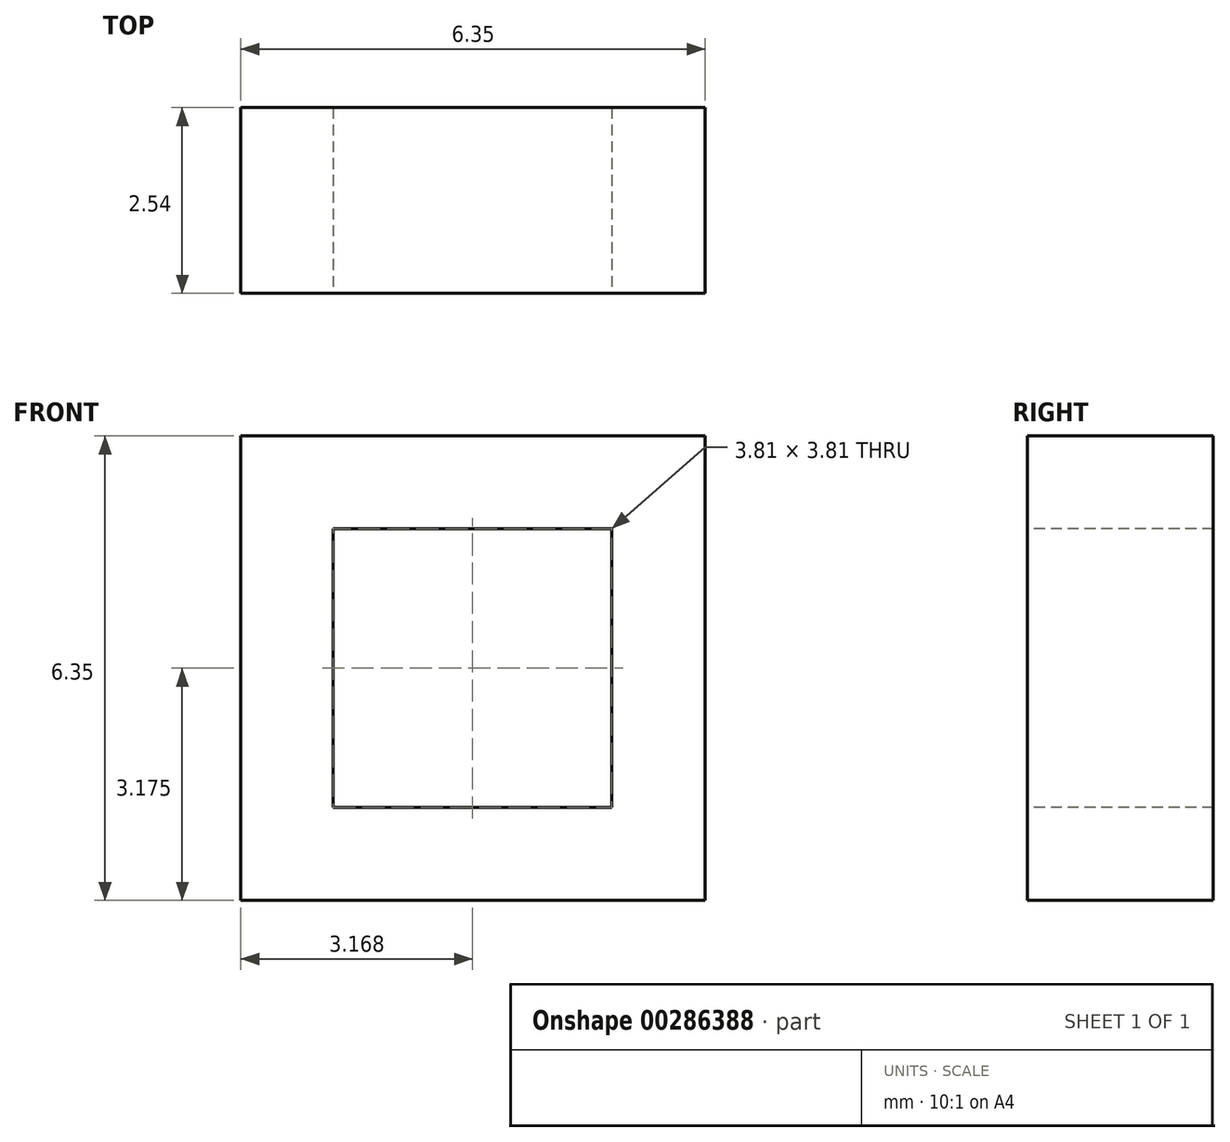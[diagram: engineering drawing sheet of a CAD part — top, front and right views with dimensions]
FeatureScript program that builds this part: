
annotation { "Feature Type Name" : "Feature", "Feature Type Description" : "" }
export const myFeature = defineFeature(function(context is Context, id is Id, definition is map)
    precondition{}
    {
        {
            var Q0;
            Q0=qCreatedBy(makeId("Front.planeOp"),FACE);
            var sketch = newSketch(context, id + "F0", { "sketchPlane" : qUnion([Q0])});
            skLineSegment(sketch, "E0.bottom", {"start": v(0, 0) * mm, "end": v(6.35, 0) * mm});
            skLineSegment(sketch, "E0.top", {"start": v(0, 6.35) * mm, "end": v(6.35, 6.35) * mm});
            skLineSegment(sketch, "E0.left", {"start": v(0, 0) * mm, "end": v(0, 6.35) * mm});
            skLineSegment(sketch, "E0.right", {"start": v(6.35, 0) * mm, "end": v(6.35, 6.35) * mm});
            skLineSegment(sketch, "E1.left", {"start": v(0, 6.35) * mm, "end": v(0, 6.35) * mm});
            skLineSegment(sketch, "E1.right", {"start": v(6.35, 6.35) * mm, "end": v(6.35, 6.35) * mm});
            skSolve(sketch);
        }
        {
            var Q0;
            Q0 = qSketchRegion(id + "F0", true);
            extrude(context, id + "F1", {"entities" : qUnion([Q0]), "depth" : 2.54 * mm});
        }
        {
            var Q0;
            Q0=makeQuery(id+"F1.opExtrude","CAP_FACE",FACE,{"disambiguationData":[OSD([sQuery(id+"F0.wireOp",EDGE,"E0.bottom"),sQuery(id+"F0.wireOp",EDGE,"E0.left"),sQuery(id+"F0.wireOp",EDGE,"E0.right"),sQuery(id+"F0.wireOp",EDGE,"E0.top")])],"isStart":false});
            var sketch = newSketch(context, id + "F2", { "sketchPlane" : qUnion([Q0])});
            skLineSegment(sketch, "E2.bottom", {"start": v(1.26, 5.08) * mm, "end": v(5.07, 5.08) * mm});
            skLineSegment(sketch, "E2.top", {"start": v(1.26, 1.27) * mm, "end": v(5.07, 1.27) * mm});
            skLineSegment(sketch, "E2.left", {"start": v(1.26, 5.08) * mm, "end": v(1.26, 1.27) * mm});
            skLineSegment(sketch, "E2.right", {"start": v(5.07, 5.08) * mm, "end": v(5.07, 1.27) * mm});
            skSolve(sketch);
        }
        {
            var Q0;
            Q0 = qSketchRegion(id + "F2", true);
            extrude(context, id + "F3", {"entities" : qUnion([Q0]), "operationType" : NewBodyOperationType.REMOVE, "oppositeDirection" : true, "depth" : 2.54 * mm});
        }
    });
